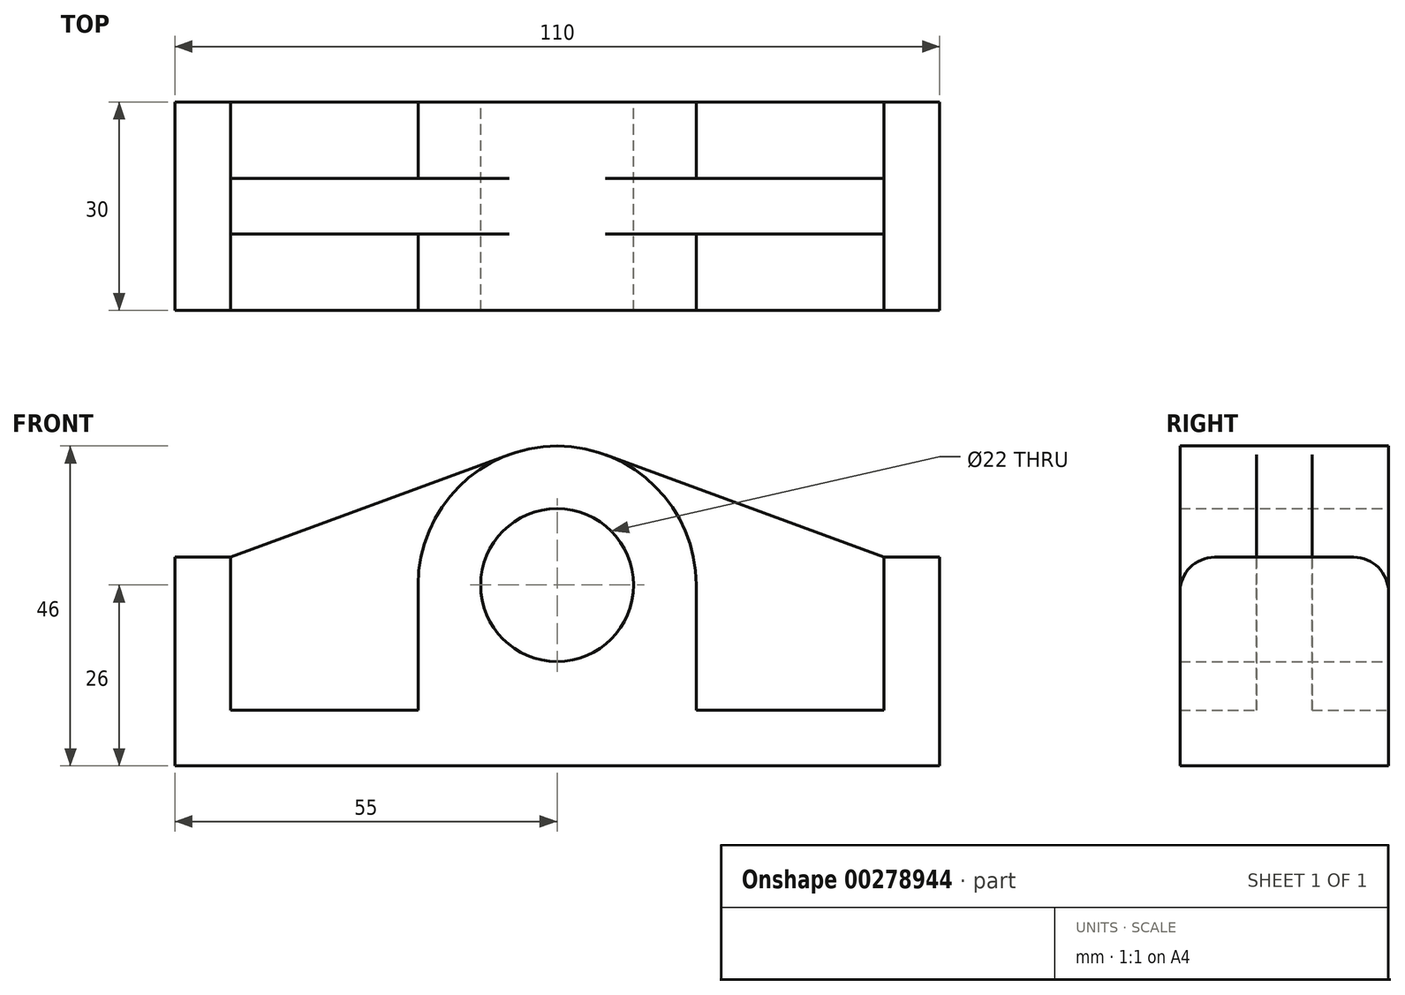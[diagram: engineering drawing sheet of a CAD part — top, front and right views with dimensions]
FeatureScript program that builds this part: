
annotation { "Feature Type Name" : "Feature", "Feature Type Description" : "" }
export const myFeature = defineFeature(function(context is Context, id is Id, definition is map)
    precondition{}
    {
        {
            var Q0;
            Q0=qCreatedBy(makeId("Front.planeOp"),FACE);
            var sketch = newSketch(context, id + "F0", { "sketchPlane" : qUnion([Q0])});
            skLineSegment(sketch, "E0", {"start": v(0, 0) * mm, "end": v(-55, 0) * mm});
            skLineSegment(sketch, "E1", {"start": v(-55, 0) * mm, "end": v(-55, 30) * mm});
            skLineSegment(sketch, "E2", {"start": v(-55, 30) * mm, "end": v(-47, 30) * mm});
            skLineSegment(sketch, "E3", {"start": v(-47, 30) * mm, "end": v(-47, 8) * mm});
            skLineSegment(sketch, "E4", {"start": v(-47, 8) * mm, "end": v(-20, 8) * mm});
            skLineSegment(sketch, "E5", {"start": v(-20, 8) * mm, "end": v(-20, 26) * mm});
            skArc(sketch, "E6", {"start": v(-20, 26) * mm, "mid": v(-14.14, 40.14) * mm, "end": v(0, 46) * mm});
            skLineSegment(sketch, "E7.MirrorCS", {"start": v(55, 0) * mm, "end": v(55, 30) * mm});
            skLineSegment(sketch, "E8.MirrorCS", {"start": v(47, 30) * mm, "end": v(47, 8) * mm});
            skLineSegment(sketch, "E9.MirrorCS", {"start": v(20, 8) * mm, "end": v(20, 26) * mm});
            skLineSegment(sketch, "E10.MirrorCS", {"start": v(55, 30) * mm, "end": v(47, 30) * mm});
            skLineSegment(sketch, "E11.MirrorCS", {"start": v(47, 8) * mm, "end": v(20, 8) * mm});
            skLineSegment(sketch, "E12.MirrorCS", {"start": v(0, 0) * mm, "end": v(55, 0) * mm});
            skArc(sketch, "E13.MirrorCS", {"start": v(20, 26) * mm, "mid": v(14.14, 40.14) * mm, "end": v(0, 46) * mm});
            skCircle(sketch, "E14", {"center": v(0, 26) * mm, "radius": 11 * mm});
            skLineSegment(sketch, "E15", {"start": v(-47, 30) * mm, "end": v(-6.91, 44.77) * mm});
            skLineSegment(sketch, "E16", {"start": v(47, 30) * mm, "end": v(6.91, 44.77) * mm});
            skSolve(sketch);
        }
        {
            var Q0;
            Q0=makeQuery(id+"F0.imprint","IMPRINT",FACE,{"disambiguationData":[TD([[makeQuery(id+"F0.imprint","IMPRINT",EDGE,{"derivedFrom":sQuery(id+"F0.wireOp",EDGE,"E0")}),-1.0]])]});
            extrude(context, id + "F1", {"entities" : qUnion([Q0]), "endBound" : BoundingType.SYMMETRIC, "depth" : 30 * mm});
        }
        {
            var Q0;
            Q0=makeQuery(id+"F0.imprint","IMPRINT",FACE,{"disambiguationData":[TD([[makeQuery(id+"F0.imprint","IMPRINT",EDGE,{"derivedFrom":sQuery(id+"F0.wireOp",EDGE,"E3")}),1.0]])]});
            var Q1;
            Q1=makeQuery(id+"F0.imprint","IMPRINT",FACE,{"disambiguationData":[TD([[makeQuery(id+"F0.imprint","IMPRINT",EDGE,{"derivedFrom":sQuery(id+"F0.wireOp",EDGE,"E8.MirrorCS")}),-1.0]])]});
            extrude(context, id + "F2", {"entities" : qUnion([Q0, Q1]), "operationType" : NewBodyOperationType.ADD, "endBound" : BoundingType.SYMMETRIC, "depth" : 8 * mm});
        }
        {
            var Q0;
            Q0=makeQuery(id+"F1.opExtrude","CAP_EDGE",EDGE,{"disambiguationData":[OSD([sQuery(id+"F0.wireOp",EDGE,"E10.MirrorCS")])],"isStart":false});
            var Q1;
            Q1=makeQuery(id+"F1.opExtrude","CAP_EDGE",EDGE,{"disambiguationData":[OSD([sQuery(id+"F0.wireOp",EDGE,"E2")])],"isStart":false});
            var Q2;
            Q2=makeQuery(id+"F1.opExtrude","CAP_EDGE",EDGE,{"disambiguationData":[OSD([sQuery(id+"F0.wireOp",EDGE,"E2")])],"isStart":true});
            var Q3;
            Q3=makeQuery(id+"F1.opExtrude","CAP_EDGE",EDGE,{"disambiguationData":[OSD([sQuery(id+"F0.wireOp",EDGE,"E10.MirrorCS")])],"isStart":true});
            fillet(context, id + "F3", {"entities" : qUnion([Q0, Q1, Q2, Q3]), "radius" : 5 * mm, "tangentPropagation" : true, "allowEdgeOverflow" : false});
        }
    });
